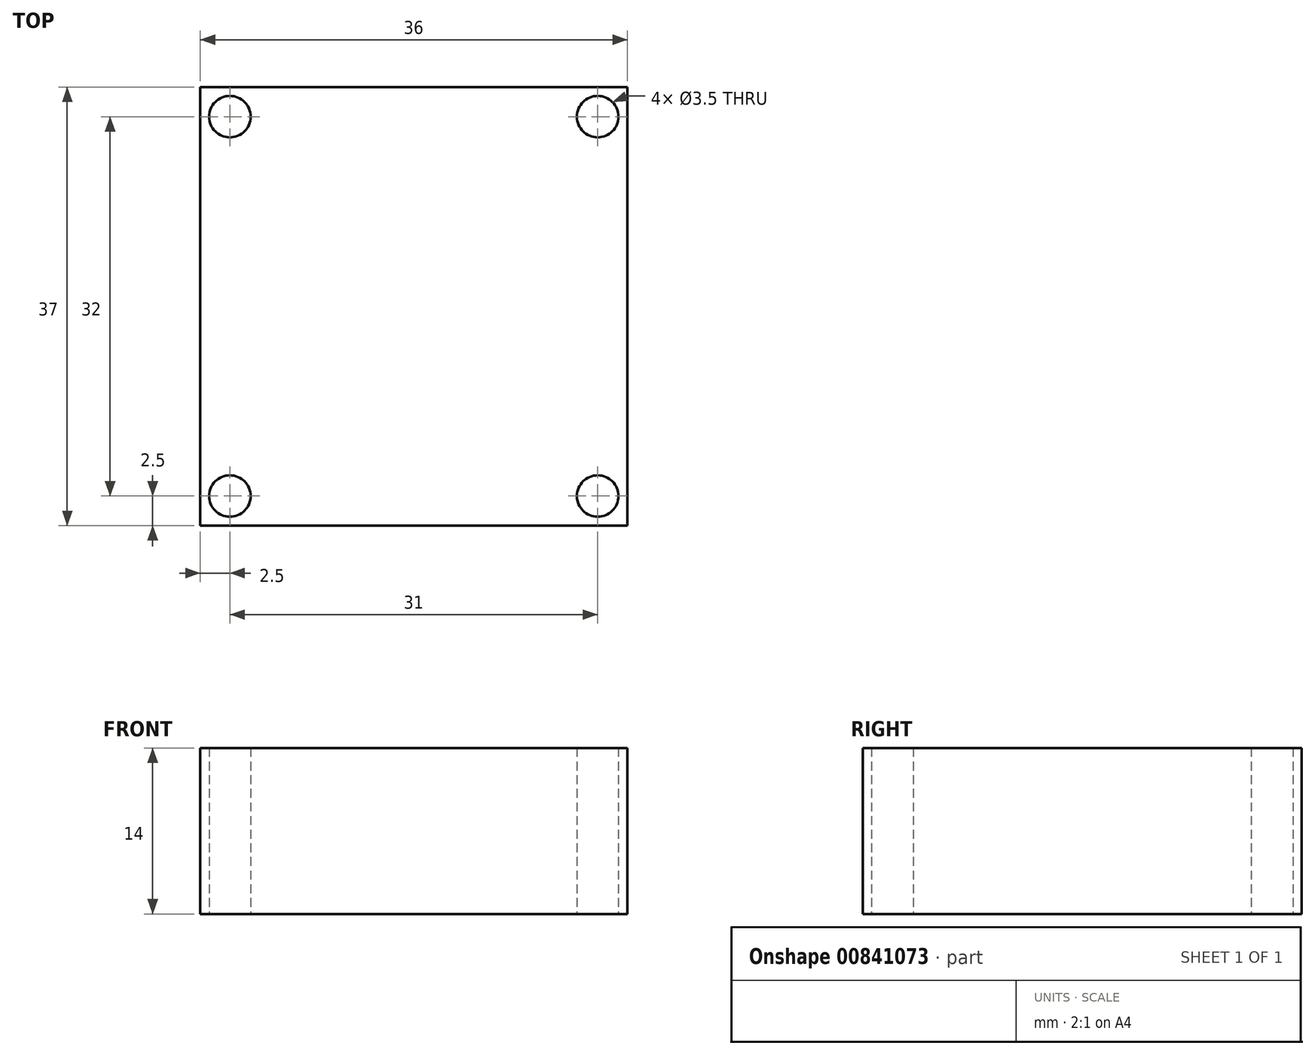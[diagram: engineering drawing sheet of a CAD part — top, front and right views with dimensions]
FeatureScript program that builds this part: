
annotation { "Feature Type Name" : "Feature", "Feature Type Description" : "" }
export const myFeature = defineFeature(function(context is Context, id is Id, definition is map)
    precondition{}
    {
        {
            var Q0;
            Q0=qCreatedBy(makeId("Top.planeOp"),FACE);
            var sketch = newSketch(context, id + "F0", { "sketchPlane" : qUnion([Q0])});
            skLineSegment(sketch, "E0.bottom", {"start": v(0, 0) * mm, "end": v(36, 0) * mm});
            skLineSegment(sketch, "E0.top", {"start": v(0, 37) * mm, "end": v(36, 37) * mm});
            skLineSegment(sketch, "E0.left", {"start": v(0, 0) * mm, "end": v(0, 37) * mm});
            skLineSegment(sketch, "E0.right", {"start": v(36, 0) * mm, "end": v(36, 37) * mm});
            skCircle(sketch, "E1", {"center": v(33.5, 34.5) * mm, "radius": 1.75 * mm});
            skCircle(sketch, "E2", {"center": v(33.5, 2.5) * mm, "radius": 1.75 * mm});
            skCircle(sketch, "E3", {"center": v(2.5, 2.5) * mm, "radius": 1.75 * mm});
            skCircle(sketch, "E4", {"center": v(2.5, 34.5) * mm, "radius": 1.75 * mm});
            skSolve(sketch);
        }
        {
            var Q0;
            Q0=makeQuery(id+"F0.imprint","IMPRINT",FACE,{"disambiguationData":[TD([[makeQuery(id+"F0.imprint","IMPRINT",EDGE,{"derivedFrom":sQuery(id+"F0.wireOp",EDGE,"E0.bottom")}),1.0]])]});
            extrude(context, id + "F1", {"entities" : qUnion([Q0]), "depth" : 14 * mm, "offsetDistance" : 25 * mm});
        }
    });
